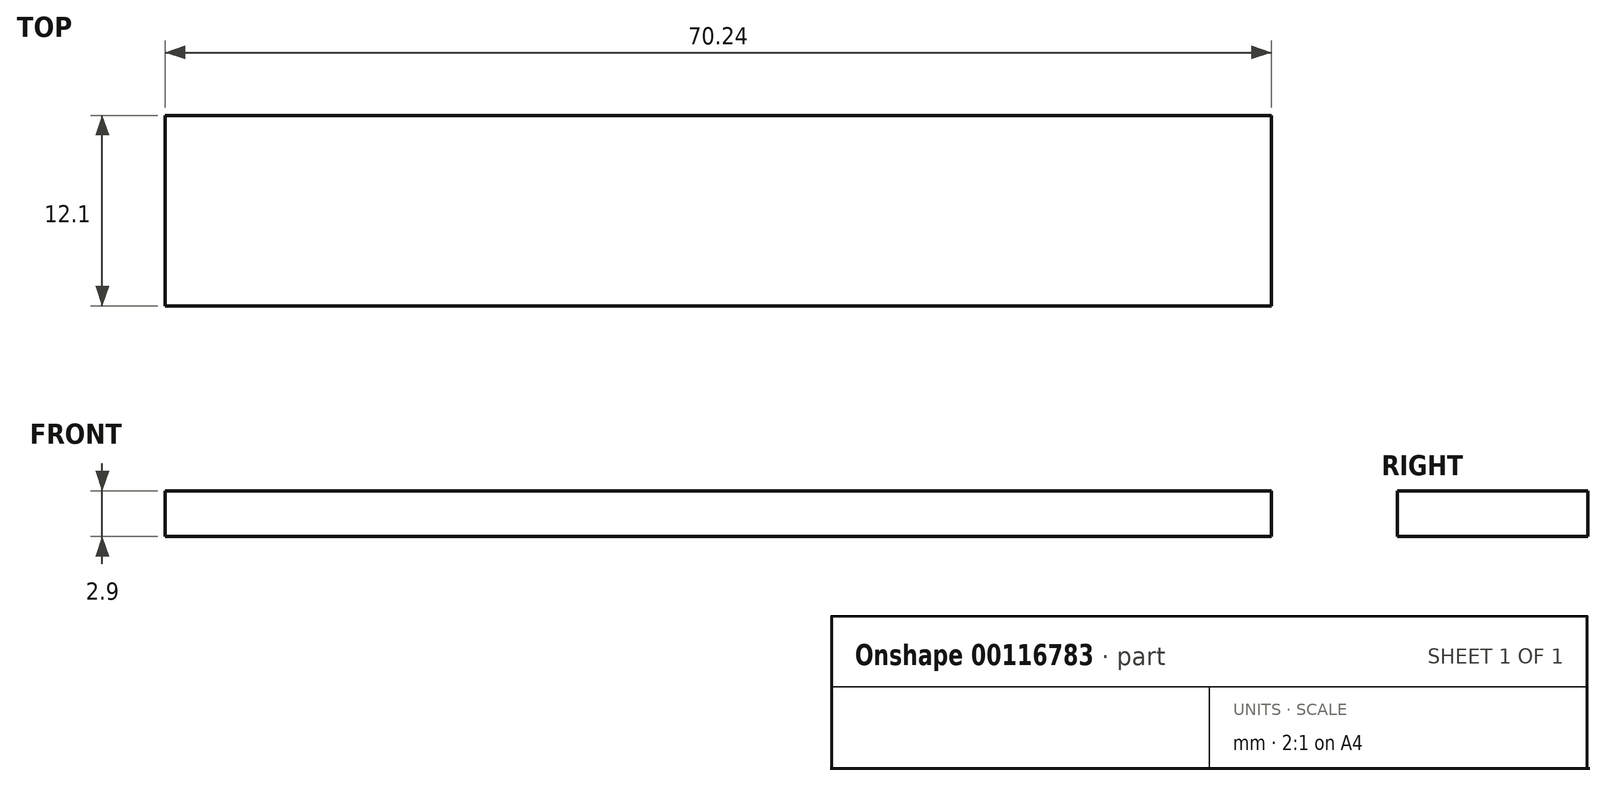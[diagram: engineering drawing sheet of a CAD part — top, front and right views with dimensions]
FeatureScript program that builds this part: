
annotation { "Feature Type Name" : "Feature", "Feature Type Description" : "" }
export const myFeature = defineFeature(function(context is Context, id is Id, definition is map)
    precondition{}
    {
        {
            var Q0;
            Q0=qCreatedBy(makeId("Top.planeOp"),FACE);
            var sketch = newSketch(context, id + "F0", { "sketchPlane" : qUnion([Q0])});
            skLineSegment(sketch, "E0.bottom", {"start": v(35.12, -6.05) * mm, "end": v(-35.12, -6.05) * mm});
            skLineSegment(sketch, "E0.top", {"start": v(35.12, 6.05) * mm, "end": v(-35.12, 6.05) * mm});
            skLineSegment(sketch, "E0.left", {"start": v(35.12, -6.05) * mm, "end": v(35.12, 6.05) * mm});
            skLineSegment(sketch, "E0.right", {"start": v(-35.12, -6.05) * mm, "end": v(-35.12, 6.05) * mm});
            skPoint(sketch, "E0.middle", {"position": v(0, 0) * mm});
            skSolve(sketch);
        }
        {
            var Q0;
            Q0 = qSketchRegion(id + "F0", true);
            extrude(context, id + "F1", {"entities" : qUnion([Q0]), "depth" : 2.9 * mm});
        }
    });
